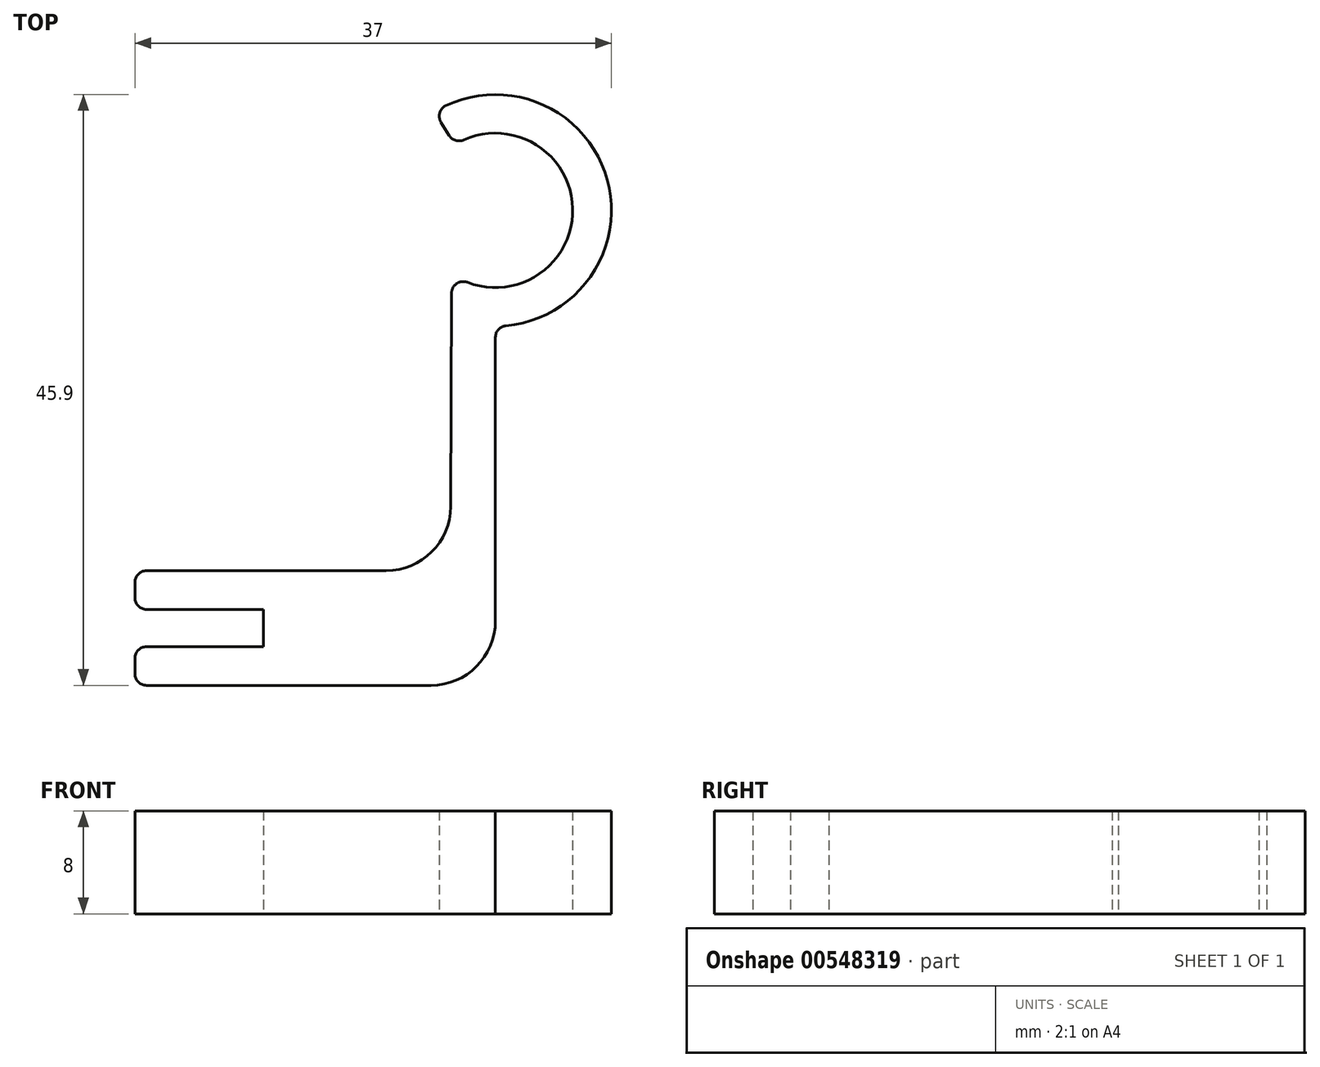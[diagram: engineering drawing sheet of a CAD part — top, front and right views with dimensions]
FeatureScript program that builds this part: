
annotation { "Feature Type Name" : "Feature", "Feature Type Description" : "" }
export const myFeature = defineFeature(function(context is Context, id is Id, definition is map)
    precondition{}
    {
        {
            var Q0;
            Q0=qCreatedBy(makeId("Top.planeOp"),FACE);
            var sketch = newSketch(context, id + "F0", { "sketchPlane" : qUnion([Q0])});
            skArc(sketch, "E0", {"start": v(12.82, -5.6) * mm, "mid": v(21, 0.15) * mm, "end": v(12.55, 5.47) * mm});
            skLineSegment(sketch, "E1.bottom", {"start": v(-12.1, -31) * mm, "end": v(-3, -31) * mm});
            skLineSegment(sketch, "E1.top", {"start": v(-12.1, -33.9) * mm, "end": v(-3, -33.9) * mm});
            skLineSegment(sketch, "E1.right", {"start": v(-3, -31) * mm, "end": v(-3, -33.9) * mm});
            skLineSegment(sketch, "E2.0", {"start": v(15, -9.86) * mm, "end": v(15, -31.9) * mm});
            skLineSegment(sketch, "E2.1", {"start": v(-13, -36.9) * mm, "end": v(10, -36.9) * mm});
            skLineSegment(sketch, "E3.0", {"start": v(-12.1, -36.9) * mm, "end": v(-0.9, -36.9) * mm});
            skLineSegment(sketch, "E4", {"start": v(-13, -36) * mm, "end": v(-13, -34.8) * mm});
            skLineSegment(sketch, "E5.0", {"start": v(-12.1, -28) * mm, "end": v(6.52, -28) * mm});
            skLineSegment(sketch, "E6.trimOffspring", {"start": v(-13, -30.1) * mm, "end": v(-13, -28.9) * mm});
            skArc(sketch, "E7.0", {"start": v(15.82, -8.96) * mm, "mid": v(23.68, 2.37) * mm, "end": v(11.16, 8.14) * mm});
            skLineSegment(sketch, "E8", {"start": v(11.52, -23.02) * mm, "end": v(11.6, -6.43) * mm});
            skLineSegment(sketch, "E9", {"start": v(11.41, 5.82) * mm, "end": v(10.78, 6.85) * mm});
            skArc(sketch, "E10.filletArc", {"start": v(11.16, 8.14) * mm, "mid": v(10.68, 7.58) * mm, "end": v(10.78, 6.85) * mm});
            skArc(sketch, "E11.filletArc", {"start": v(11.41, 5.82) * mm, "mid": v(11.91, 5.44) * mm, "end": v(12.55, 5.47) * mm});
            skArc(sketch, "E12.filletArc", {"start": v(12.82, -5.6) * mm, "mid": v(11.99, -5.69) * mm, "end": v(11.6, -6.43) * mm});
            skArc(sketch, "E13.filletArc", {"start": v(15.82, -8.96) * mm, "mid": v(15.24, -9.25) * mm, "end": v(15, -9.86) * mm});
            skPoint(sketch, "E14.newPointB", {"position": v(6, -28) * mm});
            skPoint(sketch, "E15.visualSharp", {"position": v(-13, -36.9) * mm});
            skArc(sketch, "E15.filletArc", {"start": v(-13, -36) * mm, "mid": v(-12.74, -36.64) * mm, "end": v(-12.1, -36.9) * mm});
            skPoint(sketch, "E16.visualSharp", {"position": v(-13, -33.9) * mm});
            skArc(sketch, "E16.filletArc", {"start": v(-12.1, -33.9) * mm, "mid": v(-12.74, -34.16) * mm, "end": v(-13, -34.8) * mm});
            skPoint(sketch, "E17.visualSharp", {"position": v(-13, -31) * mm});
            skArc(sketch, "E17.filletArc", {"start": v(-13, -30.1) * mm, "mid": v(-12.74, -30.74) * mm, "end": v(-12.1, -31) * mm});
            skPoint(sketch, "E18.visualSharp", {"position": v(-13, -28) * mm});
            skArc(sketch, "E18.filletArc", {"start": v(-12.1, -28) * mm, "mid": v(-12.74, -28.26) * mm, "end": v(-13, -28.9) * mm});
            skPoint(sketch, "E19.orphan", {"position": v(0, -36.9) * mm});
            skArc(sketch, "E20.filletArc", {"start": v(10, -36.9) * mm, "mid": v(13.54, -35.44) * mm, "end": v(15, -31.9) * mm});
            skArc(sketch, "E21.filletArc", {"start": v(6.52, -28) * mm, "mid": v(10.05, -26.54) * mm, "end": v(11.52, -23.02) * mm});
            skSolve(sketch);
        }
        {
            var Q0;
            Q0=makeQuery(id+"F0.imprint","IMPRINT",FACE,{"disambiguationData":[TD([[makeQuery(id+"F0.imprint","IMPRINT",EDGE,{"derivedFrom":sQuery(id+"F0.wireOp",EDGE,"E0")}),-1.0]])]});
            extrude(context, id + "F1", {"entities" : qUnion([Q0]), "depth" : 8 * mm, "offsetDistance" : 25 * mm});
        }
    });
